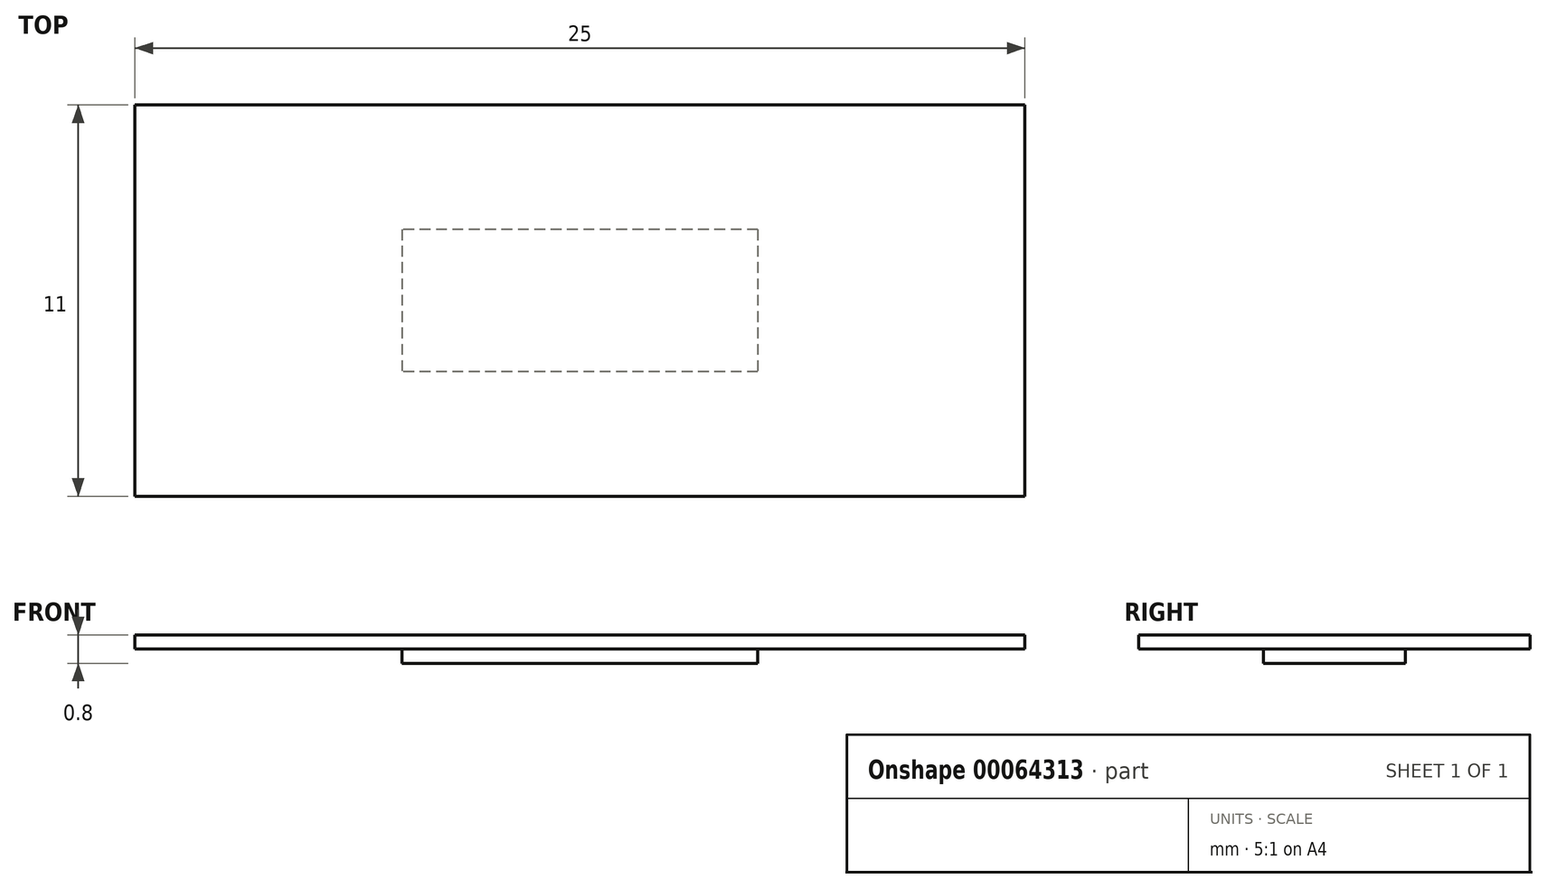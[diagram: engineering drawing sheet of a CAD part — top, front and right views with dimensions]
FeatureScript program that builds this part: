
annotation { "Feature Type Name" : "Feature", "Feature Type Description" : "" }
export const myFeature = defineFeature(function(context is Context, id is Id, definition is map)
    precondition{}
    {
        {
            var Q0;
            Q0=qCreatedBy(makeId("Top.planeOp"),FACE);
            var sketch = newSketch(context, id + "F0", { "sketchPlane" : qUnion([Q0])});
            skLineSegment(sketch, "E0.bottom", {"start": v(12.5, 5.5) * mm, "end": v(-12.5, 5.5) * mm});
            skLineSegment(sketch, "E0.top", {"start": v(12.5, -5.5) * mm, "end": v(-12.5, -5.5) * mm});
            skLineSegment(sketch, "E0.left", {"start": v(12.5, 5.5) * mm, "end": v(12.5, -5.5) * mm});
            skLineSegment(sketch, "E0.right", {"start": v(-12.5, 5.5) * mm, "end": v(-12.5, -5.5) * mm});
            skPoint(sketch, "E0.middle", {"position": v(0, 0) * mm});
            skSolve(sketch);
        }
        {
            var Q0;
            Q0 = qSketchRegion(id + "F0", true);
            extrude(context, id + "F1", {"entities" : qUnion([Q0]), "depth" : .4 * mm});
        }
        {
            var Q0;
            Q0=qCreatedBy(makeId("Top.planeOp"),FACE);
            var sketch = newSketch(context, id + "F2", { "sketchPlane" : qUnion([Q0])});
            skLineSegment(sketch, "E1.bottom", {"start": v(5, 2) * mm, "end": v(-5, 2) * mm});
            skLineSegment(sketch, "E1.top", {"start": v(5, -2) * mm, "end": v(-5, -2) * mm});
            skLineSegment(sketch, "E1.left", {"start": v(5, 2) * mm, "end": v(5, -2) * mm});
            skLineSegment(sketch, "E1.right", {"start": v(-5, 2) * mm, "end": v(-5, -2) * mm});
            skPoint(sketch, "E1.middle", {"position": v(0, 0) * mm});
            skSolve(sketch);
        }
        {
            var Q0;
            Q0 = qSketchRegion(id + "F2", true);
            extrude(context, id + "F3", {"entities" : qUnion([Q0]), "oppositeDirection" : true, "depth" : .4 * mm});
        }
    });
